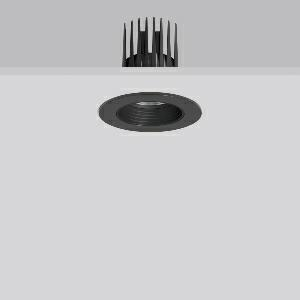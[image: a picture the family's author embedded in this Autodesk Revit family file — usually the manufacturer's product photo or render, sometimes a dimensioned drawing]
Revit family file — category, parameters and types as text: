
# Revit family: heledon_mini_e_901744_003_2_76_e02c
name_source: partatom
category: Lighting Fixtures
units: mm (PartAtom-declared; Revit-internal decimal feet)

## family parameters
Cut with Voids When Loaded = No
Host = Face
Light Source = No
Part Type = Normal
Room Calculation Point = No
Round Connector Dimension = Use Diameter
Shared = No

## types (1)
- HELEDON mini E (1 x LED Modul 927, 2000 lm, 2700)
    Apparent Load = 20 VA
    Approval mark = CE
    CIE Flux Codes = 96 100 100 100 100
    Color Rendering = 92
    Color Temperature = 2700
    Default Elevation = 1800 mm
    Description = Series: HELEDON mini
Round recessed downlight. Housing: die-cast aluminium, powder-coated. Black plastic ring and recessed LED to prevent glare from the side. Optical assembly with lens made of plastic (polycarbonate) for the best homogeneous light distribution - can be changed without tools. Best colour rendering index Ra>90. Suitable for Recessed ceiling mounting. Installation without tools thanks to spring fastening system. Including separate LED converter with connecting cable 600 mm.High quality converter without flickering and stroboscopic effect. Through-wiring box (5 pole) available as accessory. The following accessories can be mounted without use of tools: interchangeable lenses, decorative glasses, honeycomb louvre, clear and frosted diffusers, white interchangeable plastic ring. 
Colour: deep black, matt (RAL 9005)
Diameter: 124 mm
Height: 3 mm
Cut-out diameter: 114 mm
Recess height: 170 mm
Luminaire: recess height: 120 mm
Lamp: LED
Socket: without socket
Colour temperature: 2700K
Colour rendering index (CRI): 92
System power: 20 W
Rated luminous flux: 2000 lm
Luminous efficiency: 100 lm/W
Control gear: Converter, dimmable, DALI
Protection class: II
Type of protection: IP 20
    Height = 0 mm  [stored 0 ft]
    Lamp = 1 x LED Modul 927
    Lamp Light Flux = 2000 lm
    Lamp count = 1
    Length = 124 mm  [stored 0.406824 ft]
    Lifetime = 50000 h
    Luminous efficacy = 100 lm/W
    Manufacturer = RZB
    ModVariant = No
    Model = 901744.003.2.76
    Mounting Place = Ceiling
    Mounting Type = Recessed
    Number of Poles = 1
    OnlyDefault = Yes
    Power Factor = 1
    Product Name = HELEDON mini E
    Product group = Recessed downlights
    ProductGroupID = 402
    Protection Class = Protection class II
    Protection Degree = IP 20
    RLX_Detail_Level = 1
    RLX_Emergency_Light_Flux = 0 lm
    RLX_Emergency_Type = 0
    RLX_Emergency_Type_DB = No
    RlxData = <blob elided: 124281 chars, md5=981157b0>
    Socket = socket
    Standby Power = 0 W
    System Light Flux = 2000 lm
    System Power = 20 W
    Type Comments = Product without accessories
    Type Image = 901656.003.jpg
    URL = http://relux.com
    VarID = ---
    Voltage = 230 V
    Voltage Range = 220-240 V
    Weight = 0.00 kg
    Width = 0 mm  [stored 0 ft]

note: [stored X ft] marks values corroborated as IEEE doubles in the binary element streams (Revit-internal decimal feet)

## geometry (parser evidence)
native form markers: Blend x4, Sweep x10
no freeform markers — native parametric forms only
